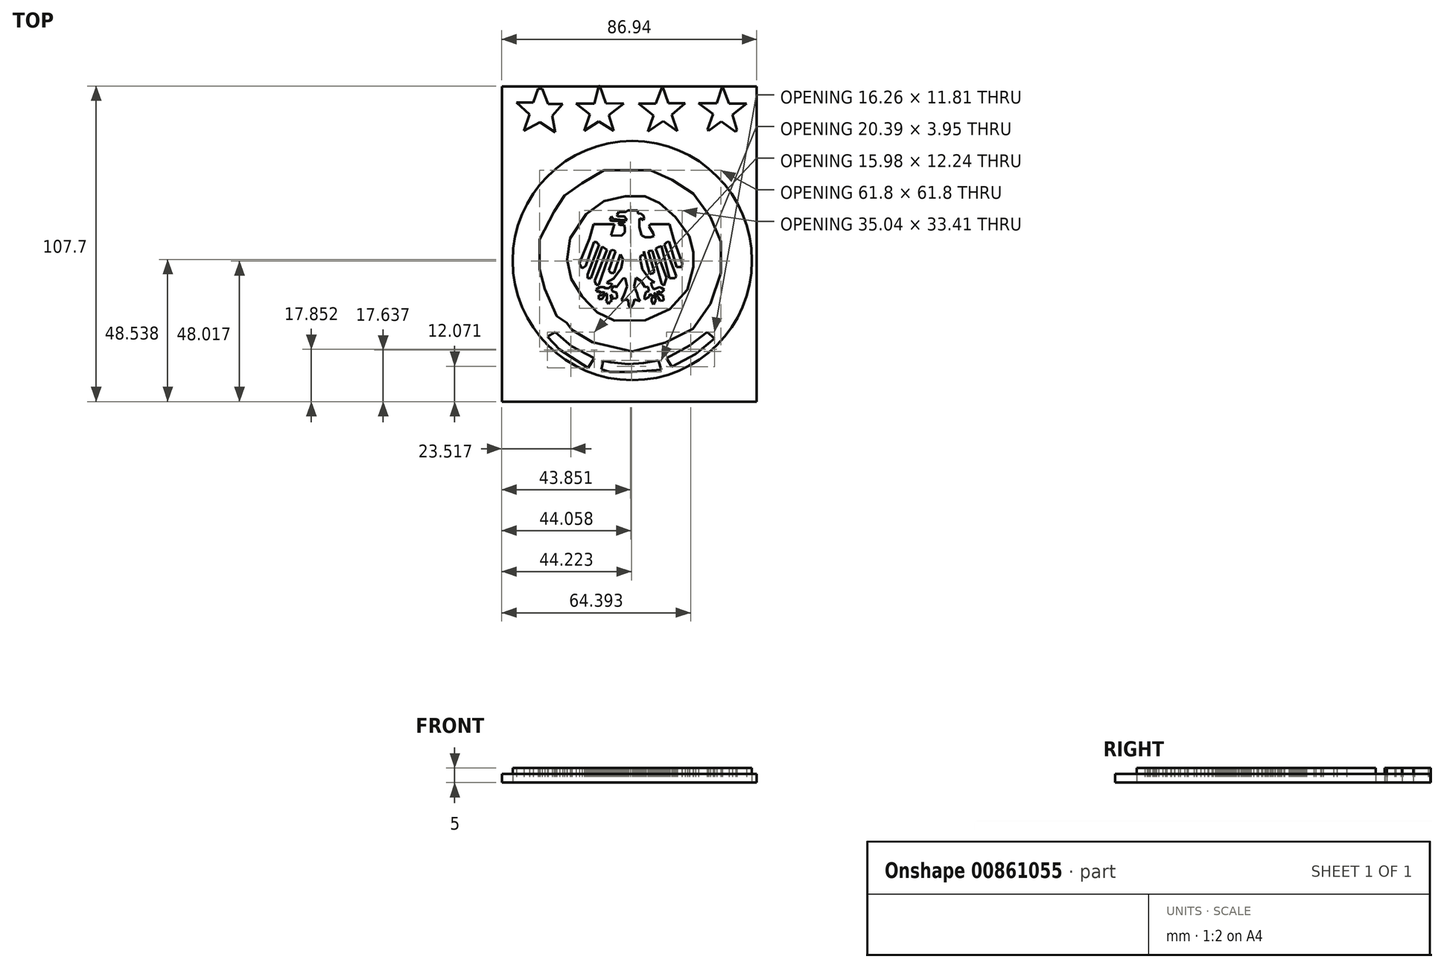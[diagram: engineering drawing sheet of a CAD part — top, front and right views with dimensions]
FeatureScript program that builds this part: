
annotation { "Feature Type Name" : "Feature", "Feature Type Description" : "" }
export const myFeature = defineFeature(function(context is Context, id is Id, definition is map)
    precondition{}
    {
        {
            var Q0;
            Q0=qCreatedBy(makeId("Top.planeOp"),FACE);
            var sketch = newSketch(context, id + "F0", { "sketchPlane" : qUnion([Q0])});
            skLineSegment(sketch, "E0", {"start": v(-17.22, 22.37) * mm, "end": v(-9.63, 26.73) * mm});
            skLineSegment(sketch, "E1", {"start": v(-9.63, 26.73) * mm, "end": v(0, 26.73) * mm});
            skLineSegment(sketch, "E2", {"start": v(0, 26.73) * mm, "end": v(6.18, 26.73) * mm});
            skLineSegment(sketch, "E3", {"start": v(6.18, 26.73) * mm, "end": v(13.6, 23.5) * mm});
            skLineSegment(sketch, "E4", {"start": v(13.6, 23.5) * mm, "end": v(20.86, 18.82) * mm});
            skLineSegment(sketch, "E5", {"start": v(20.86, 18.82) * mm, "end": v(26.67, 10.75) * mm});
            skLineSegment(sketch, "E6", {"start": v(26.67, 10.75) * mm, "end": v(30.22, 2.36) * mm});
            skLineSegment(sketch, "E7", {"start": v(30.22, 2.36) * mm, "end": v(30.22, -8.29) * mm});
            skLineSegment(sketch, "E8", {"start": v(30.22, -8.29) * mm, "end": v(26.67, -18.77) * mm});
            skLineSegment(sketch, "E9", {"start": v(26.67, -18.77) * mm, "end": v(20.7, -27.33) * mm});
            skLineSegment(sketch, "E10", {"start": v(20.7, -27.33) * mm, "end": v(11.34, -32) * mm});
            skLineSegment(sketch, "E11", {"start": v(11.34, -32) * mm, "end": v(0, -35.07) * mm});
            skLineSegment(sketch, "E12", {"start": v(0, -35.07) * mm, "end": v(-13.67, -31.84) * mm});
            skLineSegment(sketch, "E13", {"start": v(-13.67, -31.84) * mm, "end": v(-20.6, -27.65) * mm});
            skLineSegment(sketch, "E14", {"start": v(-20.6, -27.65) * mm, "end": v(-22.33, -25.26) * mm});
            skLineSegment(sketch, "E15", {"start": v(-22.33, -25.26) * mm, "end": v(-25.77, -22.97) * mm});
            skLineSegment(sketch, "E16", {"start": v(-25.77, -22.97) * mm, "end": v(-29.8, -13.77) * mm});
            skLineSegment(sketch, "E17", {"start": v(-29.8, -13.77) * mm, "end": v(-31.58, -7) * mm});
            skLineSegment(sketch, "E18", {"start": v(-31.58, -7) * mm, "end": v(-31.58, 3.17) * mm});
            skLineSegment(sketch, "E19", {"start": v(-31.58, 3.17) * mm, "end": v(-26.74, 12.69) * mm});
            skLineSegment(sketch, "E20", {"start": v(-26.74, 12.69) * mm, "end": v(-23.19, 18.17) * mm});
            skLineSegment(sketch, "E21", {"start": v(-23.19, 18.17) * mm, "end": v(-17.22, 22.37) * mm});
            skLineSegment(sketch, "E22", {"start": v(4.4, -24.42) * mm, "end": v(12.8, -20.55) * mm});
            skLineSegment(sketch, "E23", {"start": v(12.8, -20.55) * mm, "end": v(18.76, -13.93) * mm});
            skLineSegment(sketch, "E24", {"start": v(18.76, -13.93) * mm, "end": v(20.86, -6.19) * mm});
            skLineSegment(sketch, "E25", {"start": v(20.86, -6.19) * mm, "end": v(20.86, -1.19) * mm});
            skLineSegment(sketch, "E26", {"start": v(20.86, -1.19) * mm, "end": v(19.4, 4.3) * mm});
            skLineSegment(sketch, "E27", {"start": v(19.4, 4.3) * mm, "end": v(14.76, 10.75) * mm});
            skLineSegment(sketch, "E28", {"start": v(14.76, 10.75) * mm, "end": v(9.24, 15.6) * mm});
            skLineSegment(sketch, "E29", {"start": v(9.24, 15.6) * mm, "end": v(4.24, 17.85) * mm});
            skLineSegment(sketch, "E30", {"start": v(4.24, 17.85) * mm, "end": v(-2.37, 17.85) * mm});
            skLineSegment(sketch, "E31", {"start": v(-2.37, 17.85) * mm, "end": v(-9.63, 16.24) * mm});
            skLineSegment(sketch, "E32", {"start": v(-9.63, 16.24) * mm, "end": v(-15.78, 11.8) * mm});
            skLineSegment(sketch, "E33", {"start": v(-15.78, 11.8) * mm, "end": v(-21.25, 3.5) * mm});
            skLineSegment(sketch, "E34", {"start": v(-21.25, 3.5) * mm, "end": v(-22.22, -3.77) * mm});
            skLineSegment(sketch, "E35", {"start": v(-22.22, -3.77) * mm, "end": v(-20.81, -10.32) * mm});
            skLineSegment(sketch, "E36", {"start": v(-20.81, -10.32) * mm, "end": v(-17.22, -16.28) * mm});
            skLineSegment(sketch, "E37", {"start": v(-17.22, -16.28) * mm, "end": v(-11.94, -21.75) * mm});
            skLineSegment(sketch, "E38", {"start": v(-11.94, -21.75) * mm, "end": v(-6.14, -24.57) * mm});
            skLineSegment(sketch, "E39", {"start": v(-6.14, -24.57) * mm, "end": v(4.4, -24.42) * mm});
            skLineSegment(sketch, "E40", {"start": v(-7.3, 4.52) * mm, "end": v(-6.06, 8.33) * mm});
            skLineSegment(sketch, "E41", {"start": v(-6.06, 8.33) * mm, "end": v(-13.27, 8.33) * mm});
            skLineSegment(sketch, "E42", {"start": v(-13.27, 8.33) * mm, "end": v(-14.6, 3.44) * mm});
            skLineSegment(sketch, "E43", {"start": v(-14.6, 3.44) * mm, "end": v(-18, -4.93) * mm});
            skLineSegment(sketch, "E44", {"start": v(-18, -4.93) * mm, "end": v(-17.22, -6.75) * mm});
            skLineSegment(sketch, "E45", {"start": v(-17.22, -6.75) * mm, "end": v(-15.95, -5.84) * mm});
            skLineSegment(sketch, "E46", {"start": v(-15.95, -5.84) * mm, "end": v(-13.1, 2.28) * mm});
            skLineSegment(sketch, "E47", {"start": v(-13.1, 2.28) * mm, "end": v(-12.16, 2.28) * mm});
            skLineSegment(sketch, "E48", {"start": v(-12.16, 2.28) * mm, "end": v(-11.7, 1.64) * mm});
            skLineSegment(sketch, "E49", {"start": v(-11.7, 1.64) * mm, "end": v(-10.3, 0.76) * mm});
            skLineSegment(sketch, "E50", {"start": v(-10.3, 0.76) * mm, "end": v(-14.1, -10.07) * mm});
            skLineSegment(sketch, "E51", {"start": v(-14.1, -10.07) * mm, "end": v(-15.32, -10.07) * mm});
            skLineSegment(sketch, "E52", {"start": v(-15.32, -10.07) * mm, "end": v(-15.32, -8.75) * mm});
            skLineSegment(sketch, "E53", {"start": v(-15.32, -8.75) * mm, "end": v(-11.31, 1.4) * mm});
            skLineSegment(sketch, "E54", {"start": v(-11.49, -12.36) * mm, "end": v(-7.44, -0.65) * mm});
            skLineSegment(sketch, "E55", {"start": v(-7.44, -0.65) * mm, "end": v(-7.81, 0) * mm});
            skLineSegment(sketch, "E56", {"start": v(-7.81, 0) * mm, "end": v(-8.62, -0.47) * mm});
            skLineSegment(sketch, "E57", {"start": v(-8.62, -0.47) * mm, "end": v(-12.8, -10.98) * mm});
            skLineSegment(sketch, "E58", {"start": v(-12.8, -10.98) * mm, "end": v(-12.36, -12.3) * mm});
            skLineSegment(sketch, "E59", {"start": v(-12.36, -12.3) * mm, "end": v(-11.49, -12.36) * mm});
            skLineSegment(sketch, "E60", {"start": v(-10.3, 0.76) * mm, "end": v(-8.62, -0.47) * mm});
            skLineSegment(sketch, "E61", {"start": v(-5.74, -0.93) * mm, "end": v(-7.98, -7.4) * mm});
            skLineSegment(sketch, "E62", {"start": v(-7.98, -7.4) * mm, "end": v(-7.44, -8.34) * mm});
            skLineSegment(sketch, "E63", {"start": v(-7.44, -8.34) * mm, "end": v(-6.27, -8.34) * mm});
            skLineSegment(sketch, "E64", {"start": v(-6.27, -8.34) * mm, "end": v(-4.07, -1.98) * mm});
            skLineSegment(sketch, "E65", {"start": v(-4.07, -1.98) * mm, "end": v(-4.72, -0.87) * mm});
            skLineSegment(sketch, "E66", {"start": v(-4.72, -0.87) * mm, "end": v(-5.74, -0.93) * mm});
            skLineSegment(sketch, "E67", {"start": v(-7.44, -0.65) * mm, "end": v(-6.43, -0.47) * mm});
            skLineSegment(sketch, "E68", {"start": v(-6.43, -0.47) * mm, "end": v(-5.74, -0.93) * mm});
            skLineSegment(sketch, "E69", {"start": v(-4.07, -1.98) * mm, "end": v(-3.16, -3.56) * mm});
            skLineSegment(sketch, "E70", {"start": v(-3.16, -3.56) * mm, "end": v(-3.8, -6.77) * mm});
            skLineSegment(sketch, "E71", {"start": v(-3.8, -6.77) * mm, "end": v(-6.3, -10.13) * mm});
            skLineSegment(sketch, "E72", {"start": v(-6.3, -10.13) * mm, "end": v(-8.62, -11.47) * mm});
            skLineSegment(sketch, "E73", {"start": v(-8.62, -11.47) * mm, "end": v(-8.37, -11.91) * mm});
            skLineSegment(sketch, "E74", {"start": v(-8.37, -11.91) * mm, "end": v(-7.13, -11.83) * mm});
            skLineSegment(sketch, "E75", {"start": v(-7.13, -11.83) * mm, "end": v(-6.82, -12.36) * mm});
            skLineSegment(sketch, "E76", {"start": v(-6.82, -12.36) * mm, "end": v(-8.06, -13.43) * mm});
            skLineSegment(sketch, "E77", {"start": v(-8.06, -13.43) * mm, "end": v(-9.14, -13.5) * mm});
            skLineSegment(sketch, "E78", {"start": v(-9.14, -13.5) * mm, "end": v(-9.83, -13.06) * mm});
            skLineSegment(sketch, "E79", {"start": v(-9.83, -13.06) * mm, "end": v(-11.04, -13.14) * mm});
            skLineSegment(sketch, "E80", {"start": v(-11.04, -13.14) * mm, "end": v(-12.31, -13.87) * mm});
            skLineSegment(sketch, "E81", {"start": v(-12.31, -13.87) * mm, "end": v(-12.27, -14.55) * mm});
            skLineSegment(sketch, "E82", {"start": v(-12.27, -14.55) * mm, "end": v(-11.74, -14.73) * mm});
            skLineSegment(sketch, "E83", {"start": v(-11.74, -14.73) * mm, "end": v(-11.12, -14.37) * mm});
            skLineSegment(sketch, "E84", {"start": v(-11.12, -14.37) * mm, "end": v(-11.07, -15.22) * mm});
            skLineSegment(sketch, "E85", {"start": v(-11.07, -15.22) * mm, "end": v(-10.3, -14.77) * mm});
            skLineSegment(sketch, "E86", {"start": v(-10.3, -14.77) * mm, "end": v(-9.42, -15.07) * mm});
            skLineSegment(sketch, "E87", {"start": v(-9.42, -15.07) * mm, "end": v(-10.3, -15.84) * mm});
            skLineSegment(sketch, "E88", {"start": v(-10.3, -15.84) * mm, "end": v(-11.49, -15.92) * mm});
            skLineSegment(sketch, "E89", {"start": v(-11.49, -15.92) * mm, "end": v(-11.49, -17.22) * mm});
            skLineSegment(sketch, "E90", {"start": v(-11.49, -17.22) * mm, "end": v(-10.3, -17.22) * mm});
            skLineSegment(sketch, "E91", {"start": v(-10.3, -17.22) * mm, "end": v(-9.82, -16.46) * mm});
            skLineSegment(sketch, "E92", {"start": v(-9.82, -16.46) * mm, "end": v(-9.08, -15.28) * mm});
            skLineSegment(sketch, "E93", {"start": v(-9.08, -15.28) * mm, "end": v(-8.62, -15.44) * mm});
            skLineSegment(sketch, "E94", {"start": v(-8.62, -15.44) * mm, "end": v(-8.62, -17.32) * mm});
            skLineSegment(sketch, "E95", {"start": v(-8.62, -17.32) * mm, "end": v(-9, -17.94) * mm});
            skLineSegment(sketch, "E96", {"start": v(-9, -17.94) * mm, "end": v(-8.62, -18.07) * mm});
            skLineSegment(sketch, "E97", {"start": v(-8.62, -18.07) * mm, "end": v(-8.1, -18.96) * mm});
            skLineSegment(sketch, "E98", {"start": v(-8.1, -18.96) * mm, "end": v(-7.57, -18.1) * mm});
            skLineSegment(sketch, "E99", {"start": v(-7.57, -18.1) * mm, "end": v(-6.9, -17.72) * mm});
            skLineSegment(sketch, "E100", {"start": v(-6.9, -17.72) * mm, "end": v(-7.29, -17.04) * mm});
            skLineSegment(sketch, "E101", {"start": v(-7.29, -17.04) * mm, "end": v(-7.36, -15.81) * mm});
            skLineSegment(sketch, "E102", {"start": v(-7.36, -15.81) * mm, "end": v(-6.84, -16) * mm});
            skLineSegment(sketch, "E103", {"start": v(-6.84, -16) * mm, "end": v(-6.77, -17.05) * mm});
            skLineSegment(sketch, "E104", {"start": v(-6.77, -17.05) * mm, "end": v(-5.4, -16.96) * mm});
            skLineSegment(sketch, "E105", {"start": v(-5.4, -16.96) * mm, "end": v(-5.2, -16.46) * mm});
            skLineSegment(sketch, "E106", {"start": v(-5.2, -16.46) * mm, "end": v(-5.3, -15.06) * mm});
            skLineSegment(sketch, "E107", {"start": v(-5.3, -15.06) * mm, "end": v(-6.9, -14.5) * mm});
            skLineSegment(sketch, "E108", {"start": v(-6.9, -14.5) * mm, "end": v(-6.96, -13.56) * mm});
            skLineSegment(sketch, "E109", {"start": v(-6.96, -13.56) * mm, "end": v(-6.02, -12.64) * mm});
            skLineSegment(sketch, "E110", {"start": v(-6.02, -12.64) * mm, "end": v(-5.46, -13.2) * mm});
            skLineSegment(sketch, "E111", {"start": v(-5.46, -13.2) * mm, "end": v(-3.23, -10.13) * mm});
            skLineSegment(sketch, "E112", {"start": v(-3.23, -10.13) * mm, "end": v(-2.37, -10.08) * mm});
            skLineSegment(sketch, "E113", {"start": v(-2.37, -10.08) * mm, "end": v(-1.85, -12.83) * mm});
            skLineSegment(sketch, "E114", {"start": v(-1.85, -12.83) * mm, "end": v(-2.94, -16) * mm});
            skLineSegment(sketch, "E115", {"start": v(-2.94, -16) * mm, "end": v(-3.64, -17.38) * mm});
            skLineSegment(sketch, "E116", {"start": v(-3.64, -17.38) * mm, "end": v(-3.32, -17.93) * mm});
            skLineSegment(sketch, "E117", {"start": v(-3.32, -17.93) * mm, "end": v(-2.52, -17.46) * mm});
            skLineSegment(sketch, "E118", {"start": v(-2.52, -17.46) * mm, "end": v(-1.47, -17.4) * mm});
            skLineSegment(sketch, "E119", {"start": v(-1.47, -17.4) * mm, "end": v(-1.32, -19.14) * mm});
            skLineSegment(sketch, "E120", {"start": v(-1.32, -19.14) * mm, "end": v(-0.61, -20.35) * mm});
            skLineSegment(sketch, "E121", {"start": v(-0.61, -20.35) * mm, "end": v(0.18, -19.1) * mm});
            skLineSegment(sketch, "E122", {"start": v(0.18, -19.1) * mm, "end": v(0.79, -17.32) * mm});
            skLineSegment(sketch, "E123", {"start": v(0.79, -17.32) * mm, "end": v(1.62, -17.6) * mm});
            skLineSegment(sketch, "E124", {"start": v(1.62, -17.6) * mm, "end": v(2.6, -17.95) * mm});
            skLineSegment(sketch, "E125", {"start": v(2.6, -17.95) * mm, "end": v(2.02, -16.95) * mm});
            skLineSegment(sketch, "E126", {"start": v(2.02, -16.95) * mm, "end": v(1.6, -15.25) * mm});
            skLineSegment(sketch, "E127", {"start": v(1.6, -15.25) * mm, "end": v(0.66, -12.83) * mm});
            skLineSegment(sketch, "E128", {"start": v(0.66, -12.83) * mm, "end": v(1.26, -9.97) * mm});
            skLineSegment(sketch, "E129", {"start": v(1.26, -9.97) * mm, "end": v(3.04, -11.08) * mm});
            skLineSegment(sketch, "E130", {"start": v(3.04, -11.08) * mm, "end": v(4.33, -13.05) * mm});
            skLineSegment(sketch, "E131", {"start": v(4.33, -13.05) * mm, "end": v(5.27, -12.99) * mm});
            skLineSegment(sketch, "E132", {"start": v(5.27, -12.99) * mm, "end": v(5.72, -14.5) * mm});
            skLineSegment(sketch, "E133", {"start": v(5.72, -14.5) * mm, "end": v(4.67, -14.8) * mm});
            skLineSegment(sketch, "E134", {"start": v(4.67, -14.8) * mm, "end": v(4.16, -16.28) * mm});
            skLineSegment(sketch, "E135", {"start": v(4.16, -16.28) * mm, "end": v(4.23, -17.36) * mm});
            skLineSegment(sketch, "E136", {"start": v(4.23, -17.36) * mm, "end": v(5.07, -16.87) * mm});
            skLineSegment(sketch, "E137", {"start": v(5.07, -16.87) * mm, "end": v(5.82, -16.44) * mm});
            skLineSegment(sketch, "E138", {"start": v(5.82, -16.44) * mm, "end": v(5.87, -15.97) * mm});
            skLineSegment(sketch, "E139", {"start": v(5.87, -15.97) * mm, "end": v(6.12, -15.36) * mm});
            skLineSegment(sketch, "E140", {"start": v(6.12, -15.36) * mm, "end": v(6.94, -16.25) * mm});
            skLineSegment(sketch, "E141", {"start": v(6.94, -16.25) * mm, "end": v(6.62, -17.16) * mm});
            skLineSegment(sketch, "E142", {"start": v(6.62, -17.16) * mm, "end": v(6.62, -17.95) * mm});
            skLineSegment(sketch, "E143", {"start": v(6.62, -17.95) * mm, "end": v(7.24, -19.01) * mm});
            skLineSegment(sketch, "E144", {"start": v(7.24, -19.01) * mm, "end": v(7.9, -17.95) * mm});
            skLineSegment(sketch, "E145", {"start": v(7.9, -17.95) * mm, "end": v(7.98, -17.04) * mm});
            skLineSegment(sketch, "E146", {"start": v(7.98, -17.04) * mm, "end": v(7.6, -16.38) * mm});
            skLineSegment(sketch, "E147", {"start": v(7.6, -16.38) * mm, "end": v(7.38, -15.56) * mm});
            skLineSegment(sketch, "E148", {"start": v(7.38, -15.56) * mm, "end": v(8, -15.2) * mm});
            skLineSegment(sketch, "E149", {"start": v(8, -15.2) * mm, "end": v(8.78, -16.53) * mm});
            skLineSegment(sketch, "E150", {"start": v(8.78, -16.53) * mm, "end": v(9.51, -17.76) * mm});
            skLineSegment(sketch, "E151", {"start": v(9.51, -17.76) * mm, "end": v(10.68, -17.68) * mm});
            skLineSegment(sketch, "E152", {"start": v(10.68, -17.68) * mm, "end": v(10.58, -16.03) * mm});
            skLineSegment(sketch, "E153", {"start": v(10.58, -16.03) * mm, "end": v(9.15, -15.54) * mm});
            skLineSegment(sketch, "E154", {"start": v(9.15, -15.54) * mm, "end": v(8.5, -15) * mm});
            skLineSegment(sketch, "E155", {"start": v(8.5, -15) * mm, "end": v(8.8, -14.53) * mm});
            skLineSegment(sketch, "E156", {"start": v(8.8, -14.53) * mm, "end": v(9.76, -15.12) * mm});
            skLineSegment(sketch, "E157", {"start": v(9.76, -15.12) * mm, "end": v(10.93, -14.05) * mm});
            skLineSegment(sketch, "E158", {"start": v(10.93, -14.05) * mm, "end": v(9.91, -13.42) * mm});
            skLineSegment(sketch, "E159", {"start": v(9.91, -13.42) * mm, "end": v(9.2, -13.14) * mm});
            skLineSegment(sketch, "E160", {"start": v(9.2, -13.14) * mm, "end": v(7.41, -13.83) * mm});
            skLineSegment(sketch, "E161", {"start": v(7.41, -13.83) * mm, "end": v(6.6, -12.77) * mm});
            skLineSegment(sketch, "E162", {"start": v(6.6, -12.77) * mm, "end": v(6.52, -11.57) * mm});
            skLineSegment(sketch, "E163", {"start": v(6.52, -11.57) * mm, "end": v(7.66, -11.42) * mm});
            skLineSegment(sketch, "E164", {"start": v(7.66, -11.42) * mm, "end": v(5.65, -10.16) * mm});
            skLineSegment(sketch, "E165", {"start": v(5.65, -10.16) * mm, "end": v(3.42, -6.96) * mm});
            skLineSegment(sketch, "E166", {"start": v(3.42, -6.96) * mm, "end": v(2.6, -3.29) * mm});
            skLineSegment(sketch, "E167", {"start": v(2.6, -3.29) * mm, "end": v(2.95, -2.27) * mm});
            skLineSegment(sketch, "E168", {"start": v(2.95, -2.27) * mm, "end": v(3.86, -2.21) * mm});
            skLineSegment(sketch, "E169", {"start": v(3.86, -2.21) * mm, "end": v(3.86, -0.87) * mm});
            skLineSegment(sketch, "E170", {"start": v(3.86, -0.87) * mm, "end": v(5.94, -8.62) * mm});
            skLineSegment(sketch, "E171", {"start": v(5.94, -8.62) * mm, "end": v(7.18, -8.29) * mm});
            skLineSegment(sketch, "E172", {"start": v(7.18, -8.29) * mm, "end": v(7.44, -7.74) * mm});
            skLineSegment(sketch, "E173", {"start": v(7.44, -7.74) * mm, "end": v(5.4, -0.93) * mm});
            skLineSegment(sketch, "E174", {"start": v(5.4, -0.93) * mm, "end": v(4.59, -0.65) * mm});
            skLineSegment(sketch, "E175", {"start": v(4.59, -0.65) * mm, "end": v(3.86, -0.87) * mm});
            skLineSegment(sketch, "E176", {"start": v(5.4, -0.93) * mm, "end": v(6.43, -0.62) * mm});
            skLineSegment(sketch, "E177", {"start": v(6.43, -0.62) * mm, "end": v(6.88, -0.78) * mm});
            skLineSegment(sketch, "E178", {"start": v(6.88, -0.78) * mm, "end": v(10.08, -12.01) * mm});
            skLineSegment(sketch, "E179", {"start": v(10.08, -12.01) * mm, "end": v(10.74, -12.58) * mm});
            skLineSegment(sketch, "E180", {"start": v(10.74, -12.58) * mm, "end": v(11.15, -11.4) * mm});
            skLineSegment(sketch, "E181", {"start": v(11.15, -11.4) * mm, "end": v(11.68, -9.87) * mm});
            skLineSegment(sketch, "E182", {"start": v(11.68, -9.87) * mm, "end": v(7.98, 0) * mm});
            skLineSegment(sketch, "E183", {"start": v(7.98, 0) * mm, "end": v(7.4, 0.2) * mm});
            skLineSegment(sketch, "E184", {"start": v(7.4, 0.2) * mm, "end": v(6.88, -0.74) * mm});
            skLineSegment(sketch, "E185", {"start": v(7.98, 0) * mm, "end": v(8.89, 0.64) * mm});
            skLineSegment(sketch, "E186", {"start": v(8.89, 0.64) * mm, "end": v(9.42, 0.64) * mm});
            skLineSegment(sketch, "E187", {"start": v(9.42, 0.64) * mm, "end": v(9.92, 0.95) * mm});
            skLineSegment(sketch, "E188", {"start": v(9.92, 0.95) * mm, "end": v(12.65, -10.1) * mm});
            skLineSegment(sketch, "E189", {"start": v(12.65, -10.1) * mm, "end": v(14.57, -10.1) * mm});
            skLineSegment(sketch, "E190", {"start": v(14.57, -10.1) * mm, "end": v(15.02, -9.3) * mm});
            skLineSegment(sketch, "E191", {"start": v(15.02, -9.3) * mm, "end": v(10.9, 1.36) * mm});
            skLineSegment(sketch, "E192", {"start": v(10.9, 1.36) * mm, "end": v(9.92, 0.95) * mm});
            skLineSegment(sketch, "E193", {"start": v(10.9, 1.36) * mm, "end": v(11.74, 2.2) * mm});
            skLineSegment(sketch, "E194", {"start": v(11.74, 2.2) * mm, "end": v(12.57, 2.41) * mm});
            skLineSegment(sketch, "E195", {"start": v(12.57, 2.41) * mm, "end": v(15.04, -6.3) * mm});
            skLineSegment(sketch, "E196", {"start": v(15.04, -6.3) * mm, "end": v(16.83, -6.3) * mm});
            skLineSegment(sketch, "E197", {"start": v(16.83, -6.3) * mm, "end": v(17.05, -4.92) * mm});
            skLineSegment(sketch, "E198", {"start": v(17.05, -4.92) * mm, "end": v(14.07, 3.34) * mm});
            skLineSegment(sketch, "E199", {"start": v(14.07, 3.34) * mm, "end": v(13.19, 3.34) * mm});
            skLineSegment(sketch, "E200", {"start": v(13.19, 3.34) * mm, "end": v(12.57, 2.41) * mm});
            skLineSegment(sketch, "E201", {"start": v(14.07, 3.34) * mm, "end": v(12.64, 8.38) * mm});
            skLineSegment(sketch, "E202", {"start": v(12.64, 8.38) * mm, "end": v(6.11, 8.38) * mm});
            skLineSegment(sketch, "E203", {"start": v(6.11, 8.38) * mm, "end": v(5.68, 7.61) * mm});
            skLineSegment(sketch, "E204", {"start": v(5.68, 7.61) * mm, "end": v(7.04, 5.36) * mm});
            skLineSegment(sketch, "E205", {"start": v(7.04, 5.36) * mm, "end": v(7.35, 4.24) * mm});
            skLineSegment(sketch, "E206", {"start": v(7.35, 4.24) * mm, "end": v(6.21, 3.91) * mm});
            skLineSegment(sketch, "E207", {"start": v(6.21, 3.91) * mm, "end": v(4.41, 3.91) * mm});
            skLineSegment(sketch, "E208", {"start": v(4.41, 3.91) * mm, "end": v(3.21, 4.5) * mm});
            skLineSegment(sketch, "E209", {"start": v(3.21, 4.5) * mm, "end": v(2.4, 7.36) * mm});
            skLineSegment(sketch, "E210", {"start": v(2.4, 7.36) * mm, "end": v(2.4, 9.9) * mm});
            skLineSegment(sketch, "E211", {"start": v(2.4, 9.9) * mm, "end": v(2.69, 10.45) * mm});
            skLineSegment(sketch, "E212", {"start": v(2.69, 10.45) * mm, "end": v(3.21, 10.17) * mm});
            skLineSegment(sketch, "E213", {"start": v(3.21, 10.17) * mm, "end": v(3.78, 9.8) * mm});
            skLineSegment(sketch, "E214", {"start": v(3.78, 9.8) * mm, "end": v(4.05, 10.26) * mm});
            skLineSegment(sketch, "E215", {"start": v(4.05, 10.26) * mm, "end": v(3.78, 11.33) * mm});
            skLineSegment(sketch, "E216", {"start": v(3.78, 11.33) * mm, "end": v(2.84, 12.08) * mm});
            skLineSegment(sketch, "E217", {"start": v(2.84, 12.08) * mm, "end": v(2.08, 11.87) * mm});
            skLineSegment(sketch, "E218", {"start": v(2.08, 11.87) * mm, "end": v(1.74, 13.05) * mm});
            skLineSegment(sketch, "E219", {"start": v(1.74, 13.05) * mm, "end": v(-1.54, 13.05) * mm});
            skLineSegment(sketch, "E220", {"start": v(-1.54, 13.05) * mm, "end": v(-2.19, 12.58) * mm});
            skLineSegment(sketch, "E221", {"start": v(-2.19, 12.58) * mm, "end": v(-4.56, 12.58) * mm});
            skLineSegment(sketch, "E222", {"start": v(-4.56, 12.58) * mm, "end": v(-5.25, 11.55) * mm});
            skLineSegment(sketch, "E223", {"start": v(-5.25, 11.55) * mm, "end": v(-5.08, 10.96) * mm});
            skLineSegment(sketch, "E224", {"start": v(-5.08, 10.96) * mm, "end": v(-2.71, 10.96) * mm});
            skLineSegment(sketch, "E225", {"start": v(-2.71, 10.96) * mm, "end": v(-1.76, 9.8) * mm});
            skLineSegment(sketch, "E226", {"start": v(-1.76, 9.8) * mm, "end": v(-2.93, 8.83) * mm});
            skLineSegment(sketch, "E227", {"start": v(-2.93, 8.83) * mm, "end": v(-4.4, 8.83) * mm});
            skLineSegment(sketch, "E228", {"start": v(-4.4, 8.83) * mm, "end": v(-4.65, 8.4) * mm});
            skLineSegment(sketch, "E229", {"start": v(-4.65, 8.4) * mm, "end": v(-4.12, 8.05) * mm});
            skLineSegment(sketch, "E230", {"start": v(-4.12, 8.05) * mm, "end": v(-2.8, 8.05) * mm});
            skLineSegment(sketch, "E231", {"start": v(-2.8, 8.05) * mm, "end": v(-2.53, 7.1) * mm});
            skLineSegment(sketch, "E232", {"start": v(-2.53, 7.1) * mm, "end": v(-2.53, 5.6) * mm});
            skLineSegment(sketch, "E233", {"start": v(-2.53, 5.6) * mm, "end": v(-3.64, 4.4) * mm});
            skLineSegment(sketch, "E234", {"start": v(-3.64, 4.4) * mm, "end": v(-7.3, 4.52) * mm});
            skLineSegment(sketch, "E235", {"start": v(-31.97, -27.06) * mm, "end": v(-36.45, -19.71) * mm});
            skLineSegment(sketch, "E236", {"start": v(-36.45, -19.71) * mm, "end": v(-39.2, -7.55) * mm});
            skLineSegment(sketch, "E237", {"start": v(-39.2, -7.55) * mm, "end": v(-39.2, 6.22) * mm});
            skLineSegment(sketch, "E238", {"start": v(-39.2, 6.22) * mm, "end": v(-32.9, 19.3) * mm});
            skLineSegment(sketch, "E239", {"start": v(-32.9, 19.3) * mm, "end": v(-22.06, 30.27) * mm});
            skLineSegment(sketch, "E240", {"start": v(-22.06, 30.27) * mm, "end": v(-9.75, 35.36) * mm});
            skLineSegment(sketch, "E241", {"start": v(-9.75, 35.36) * mm, "end": v(2.69, 35.36) * mm});
            skLineSegment(sketch, "E242", {"start": v(2.69, 35.36) * mm, "end": v(10.35, 34.57) * mm});
            skLineSegment(sketch, "E243", {"start": v(10.35, 34.57) * mm, "end": v(20.74, 29.6) * mm});
            skLineSegment(sketch, "E244", {"start": v(20.74, 29.6) * mm, "end": v(33.27, 18.34) * mm});
            skLineSegment(sketch, "E245", {"start": v(33.27, 18.34) * mm, "end": v(37.75, 5.8) * mm});
            skLineSegment(sketch, "E246", {"start": v(37.75, 5.8) * mm, "end": v(38.78, -8.33) * mm});
            skLineSegment(sketch, "E247", {"start": v(29.6, -26.71) * mm, "end": v(26.83, -25.33) * mm});
            skLineSegment(sketch, "E248", {"start": v(26.83, -25.33) * mm, "end": v(32.58, -17.52) * mm});
            skLineSegment(sketch, "E249", {"start": v(32.58, -17.52) * mm, "end": v(34.53, -11.52) * mm});
            skLineSegment(sketch, "E250", {"start": v(34.53, -11.52) * mm, "end": v(35.55, -1.59) * mm});
            skLineSegment(sketch, "E251", {"start": v(35.55, -1.59) * mm, "end": v(33.72, 8.33) * mm});
            skLineSegment(sketch, "E252", {"start": v(33.72, 8.33) * mm, "end": v(28.33, 18.3) * mm});
            skLineSegment(sketch, "E253", {"start": v(28.33, 18.3) * mm, "end": v(18.76, 27.85) * mm});
            skLineSegment(sketch, "E254", {"start": v(18.76, 27.85) * mm, "end": v(7.73, 31.45) * mm});
            skLineSegment(sketch, "E255", {"start": v(7.73, 31.45) * mm, "end": v(-3.64, 32.89) * mm});
            skLineSegment(sketch, "E256", {"start": v(-3.64, 32.89) * mm, "end": v(-12.76, 30.46) * mm});
            skLineSegment(sketch, "E257", {"start": v(-12.76, 30.46) * mm, "end": v(-22.58, 24.98) * mm});
            skLineSegment(sketch, "E258", {"start": v(-22.58, 24.98) * mm, "end": v(-30.4, 16.64) * mm});
            skLineSegment(sketch, "E259", {"start": v(-30.4, 16.64) * mm, "end": v(-35.04, 6.93) * mm});
            skLineSegment(sketch, "E260", {"start": v(-35.04, 6.93) * mm, "end": v(-36.4, -6.12) * mm});
            skLineSegment(sketch, "E261", {"start": v(-36.4, -6.12) * mm, "end": v(-34.05, -16.46) * mm});
            skLineSegment(sketch, "E262", {"start": v(-34.05, -16.46) * mm, "end": v(-28.49, -25.58) * mm});
            skLineSegment(sketch, "E263", {"start": v(-28.49, -25.58) * mm, "end": v(-31.97, -27.06) * mm});
            skLineSegment(sketch, "E264", {"start": v(38.78, -8.33) * mm, "end": v(37.4, -15.3) * mm});
            skLineSegment(sketch, "E265", {"start": v(37.4, -15.3) * mm, "end": v(32.74, -23.82) * mm});
            skLineSegment(sketch, "E266", {"start": v(32.74, -23.82) * mm, "end": v(30.77, -27.59) * mm});
            skLineSegment(sketch, "E267", {"start": v(30.77, -27.59) * mm, "end": v(29.6, -26.71) * mm});
            skLineSegment(sketch, "E268", {"start": v(-26.33, -28.44) * mm, "end": v(-29, -29.99) * mm});
            skLineSegment(sketch, "E269", {"start": v(-29, -29.99) * mm, "end": v(-24.73, -34.5) * mm});
            skLineSegment(sketch, "E270", {"start": v(-24.73, -34.5) * mm, "end": v(-15.16, -40.67) * mm});
            skLineSegment(sketch, "E271", {"start": v(-15.16, -40.67) * mm, "end": v(-13.02, -37.36) * mm});
            skLineSegment(sketch, "E272", {"start": v(-13.02, -37.36) * mm, "end": v(-20.75, -33.34) * mm});
            skLineSegment(sketch, "E273", {"start": v(-20.75, -33.34) * mm, "end": v(-26.33, -28.44) * mm});
            skLineSegment(sketch, "E274", {"start": v(-9.92, -38.2) * mm, "end": v(-10.5, -41.12) * mm});
            skLineSegment(sketch, "E275", {"start": v(-10.5, -41.12) * mm, "end": v(-7.61, -42.1) * mm});
            skLineSegment(sketch, "E276", {"start": v(-7.61, -42.1) * mm, "end": v(0, -42.1) * mm});
            skLineSegment(sketch, "E277", {"start": v(0, -42.1) * mm, "end": v(9.89, -41.35) * mm});
            skLineSegment(sketch, "E278", {"start": v(9.89, -41.35) * mm, "end": v(8.87, -38.14) * mm});
            skLineSegment(sketch, "E279", {"start": v(8.87, -38.14) * mm, "end": v(3.85, -39.07) * mm});
            skLineSegment(sketch, "E280", {"start": v(3.85, -39.07) * mm, "end": v(-1.33, -39.36) * mm});
            skLineSegment(sketch, "E281", {"start": v(-1.33, -39.36) * mm, "end": v(-7.4, -38.74) * mm});
            skLineSegment(sketch, "E282", {"start": v(-7.4, -38.74) * mm, "end": v(-9.92, -38.2) * mm});
            skLineSegment(sketch, "E283", {"start": v(11.73, -37.32) * mm, "end": v(13.43, -40.24) * mm});
            skLineSegment(sketch, "E284", {"start": v(13.43, -40.24) * mm, "end": v(21.54, -36) * mm});
            skLineSegment(sketch, "E285", {"start": v(21.54, -36) * mm, "end": v(28, -30.67) * mm});
            skLineSegment(sketch, "E286", {"start": v(28, -30.67) * mm, "end": v(25.45, -28.44) * mm});
            skLineSegment(sketch, "E287", {"start": v(25.45, -28.44) * mm, "end": v(19.6, -33.05) * mm});
            skLineSegment(sketch, "E288", {"start": v(19.6, -33.05) * mm, "end": v(11.73, -37.32) * mm});
            skLineSegment(sketch, "E289", {"start": v(-32.15, 54.56) * mm, "end": v(-33.75, 49.83) * mm});
            skLineSegment(sketch, "E290", {"start": v(-33.75, 49.83) * mm, "end": v(-39.52, 49.83) * mm});
            skLineSegment(sketch, "E291", {"start": v(-39.52, 49.83) * mm, "end": v(-35.01, 45.88) * mm});
            skLineSegment(sketch, "E292", {"start": v(-35.01, 45.88) * mm, "end": v(-36.93, 40.22) * mm});
            skLineSegment(sketch, "E293", {"start": v(-36.93, 40.22) * mm, "end": v(-31.55, 43.14) * mm});
            skLineSegment(sketch, "E294", {"start": v(-31.55, 43.14) * mm, "end": v(-26.33, 39.78) * mm});
            skLineSegment(sketch, "E295", {"start": v(-26.33, 39.78) * mm, "end": v(-27.36, 45.36) * mm});
            skLineSegment(sketch, "E296", {"start": v(-27.36, 45.36) * mm, "end": v(-23.82, 49.39) * mm});
            skLineSegment(sketch, "E297", {"start": v(-23.82, 49.39) * mm, "end": v(-28.67, 49.39) * mm});
            skLineSegment(sketch, "E298", {"start": v(-28.67, 49.39) * mm, "end": v(-30.72, 54.56) * mm});
            skLineSegment(sketch, "E299", {"start": v(-30.72, 54.56) * mm, "end": v(-32.15, 54.56) * mm});
            skLineSegment(sketch, "E300", {"start": v(-11.4, 55.5) * mm, "end": v(-13, 49.47) * mm});
            skLineSegment(sketch, "E301", {"start": v(-13, 49.47) * mm, "end": v(-19.23, 49.47) * mm});
            skLineSegment(sketch, "E302", {"start": v(-19.23, 49.47) * mm, "end": v(-14.5, 45.8) * mm});
            skLineSegment(sketch, "E303", {"start": v(-14.5, 45.8) * mm, "end": v(-16.39, 40.23) * mm});
            skLineSegment(sketch, "E304", {"start": v(-16.39, 40.23) * mm, "end": v(-11.45, 43.47) * mm});
            skLineSegment(sketch, "E305", {"start": v(-11.45, 43.47) * mm, "end": v(-6.37, 40.2) * mm});
            skLineSegment(sketch, "E306", {"start": v(-6.37, 40.2) * mm, "end": v(-8.06, 45.57) * mm});
            skLineSegment(sketch, "E307", {"start": v(-8.06, 45.57) * mm, "end": v(-2.88, 49.45) * mm});
            skLineSegment(sketch, "E308", {"start": v(-2.88, 49.45) * mm, "end": v(-9.07, 49.64) * mm});
            skLineSegment(sketch, "E309", {"start": v(-9.07, 49.64) * mm, "end": v(-11.04, 55.51) * mm});
            skLineSegment(sketch, "E310", {"start": v(-11.04, 55.51) * mm, "end": v(-11.4, 55.5) * mm});
            skLineSegment(sketch, "E311", {"start": v(10.23, 55.5) * mm, "end": v(12.24, 49.67) * mm});
            skLineSegment(sketch, "E312", {"start": v(12.24, 49.67) * mm, "end": v(18.04, 49.67) * mm});
            skLineSegment(sketch, "E313", {"start": v(18.04, 49.67) * mm, "end": v(13.45, 45.7) * mm});
            skLineSegment(sketch, "E314", {"start": v(13.45, 45.7) * mm, "end": v(15.33, 40.07) * mm});
            skLineSegment(sketch, "E315", {"start": v(15.33, 40.07) * mm, "end": v(10.52, 43.56) * mm});
            skLineSegment(sketch, "E316", {"start": v(10.52, 43.56) * mm, "end": v(5.33, 39.96) * mm});
            skLineSegment(sketch, "E317", {"start": v(5.33, 39.96) * mm, "end": v(7.2, 45.48) * mm});
            skLineSegment(sketch, "E318", {"start": v(7.2, 45.48) * mm, "end": v(2.1, 49.45) * mm});
            skLineSegment(sketch, "E319", {"start": v(2.1, 49.45) * mm, "end": v(8.02, 49.45) * mm});
            skLineSegment(sketch, "E320", {"start": v(8.02, 49.45) * mm, "end": v(10.23, 55.5) * mm});
            skLineSegment(sketch, "E321", {"start": v(30.77, 55.5) * mm, "end": v(28.77, 49.59) * mm});
            skLineSegment(sketch, "E322", {"start": v(28.77, 49.59) * mm, "end": v(22.56, 49.59) * mm});
            skLineSegment(sketch, "E323", {"start": v(22.56, 49.59) * mm, "end": v(27.5, 45.98) * mm});
            skLineSegment(sketch, "E324", {"start": v(27.5, 45.98) * mm, "end": v(25.67, 40.57) * mm});
            skLineSegment(sketch, "E325", {"start": v(25.67, 40.57) * mm, "end": v(26, 40.27) * mm});
            skLineSegment(sketch, "E326", {"start": v(26, 40.27) * mm, "end": v(30.3, 43.4) * mm});
            skLineSegment(sketch, "E327", {"start": v(30.3, 43.4) * mm, "end": v(35.29, 39.9) * mm});
            skLineSegment(sketch, "E328", {"start": v(35.29, 39.9) * mm, "end": v(35.71, 40.55) * mm});
            skLineSegment(sketch, "E329", {"start": v(35.71, 40.55) * mm, "end": v(34.09, 45.74) * mm});
            skLineSegment(sketch, "E330", {"start": v(34.09, 45.74) * mm, "end": v(39, 49.45) * mm});
            skLineSegment(sketch, "E331", {"start": v(39, 49.45) * mm, "end": v(33.02, 49.45) * mm});
            skLineSegment(sketch, "E332", {"start": v(33.02, 49.45) * mm, "end": v(30.77, 55.5) * mm});
            skCircle(sketch, "E333", {"center": v(0, -4.06) * mm, "radius": 40.81 * mm});
            skLineSegment(sketch, "E334", {"start": v(-1.76, 11.48) * mm, "end": v(-0.87, 11.28) * mm});
            skLineSegment(sketch, "E335", {"start": v(-0.87, 11.28) * mm, "end": v(-0.36, 11.69) * mm});
            skLineSegment(sketch, "E336", {"start": v(-0.36, 11.69) * mm, "end": v(-0.75, 12.17) * mm});
            skLineSegment(sketch, "E337", {"start": v(-0.75, 12.17) * mm, "end": v(-1.76, 11.97) * mm});
            skLineSegment(sketch, "E338", {"start": v(-1.76, 11.97) * mm, "end": v(-1.76, 11.48) * mm});
            skLineSegment(sketch, "E339", {"start": v(-3.07, 9.8) * mm, "end": v(-6.5, 10.1) * mm});
            skLineSegment(sketch, "E340", {"start": v(-6.5, 10.1) * mm, "end": v(-7.08, 11.06) * mm});
            skLineSegment(sketch, "E341", {"start": v(-7.08, 11.06) * mm, "end": v(-7.58, 9.9) * mm});
            skLineSegment(sketch, "E342", {"start": v(-7.58, 9.9) * mm, "end": v(-7, 9.5) * mm});
            skLineSegment(sketch, "E343", {"start": v(-7, 9.5) * mm, "end": v(-3.13, 9.28) * mm});
            skLineSegment(sketch, "E344", {"start": v(-3.07, 9.8) * mm, "end": v(-3.13, 9.28) * mm});
            skLineSegment(sketch, "E345", {"start": v(-3.07, 9.8) * mm, "end": v(-1.76, 9.8) * mm});
            skLineSegment(sketch, "E346", {"start": v(-3.13, 9.28) * mm, "end": v(-2.44, 9.24) * mm});
            skLineSegment(sketch, "E347", {"start": v(-2.44, 9.24) * mm, "end": v(-1.76, 9.8) * mm});
            skSolve(sketch);
        }
        {
            var Q0;
            Q0 = qSketchRegion(id + "F0", true);
            var Q1;
            Q1=makeQuery(id+"F0.imprint","IMPRINT",FACE,{"disambiguationData":[TD([[makeQuery(id+"F0.imprint","IMPRINT",EDGE,{"derivedFrom":sQuery(id+"F0.wireOp",EDGE,"E22")}),1.0]])]});
            extrude(context, id + "F1", {"entities" : qUnion([Q0, Q1]), "depth" : 5 * mm, "offsetDistance" : 25 * mm});
        }
        {
            var Q0;
            Q0=qCreatedBy(makeId("Top.planeOp"),FACE);
            var sketch = newSketch(context, id + "F2", { "sketchPlane" : qUnion([Q0])});
            skLineSegment(sketch, "E348", {"start": v(-44.53, 55.36) * mm, "end": v(42.41, 55.36) * mm});
            skLineSegment(sketch, "E349", {"start": v(42.41, 55.36) * mm, "end": v(42.41, -52.2) * mm});
            skLineSegment(sketch, "E350", {"start": v(42.41, -52.2) * mm, "end": v(-44.53, -52.2) * mm});
            skLineSegment(sketch, "E351", {"start": v(-44.53, -52.2) * mm, "end": v(-44.53, 55.36) * mm});
            skSolve(sketch);
        }
        {
            var Q0;
            Q0 = qSketchRegion(id + "F2", true);
            extrude(context, id + "F3", {"entities" : qUnion([Q0]), "depth" : 3 * mm, "offsetDistance" : 25 * mm});
        }
    });
